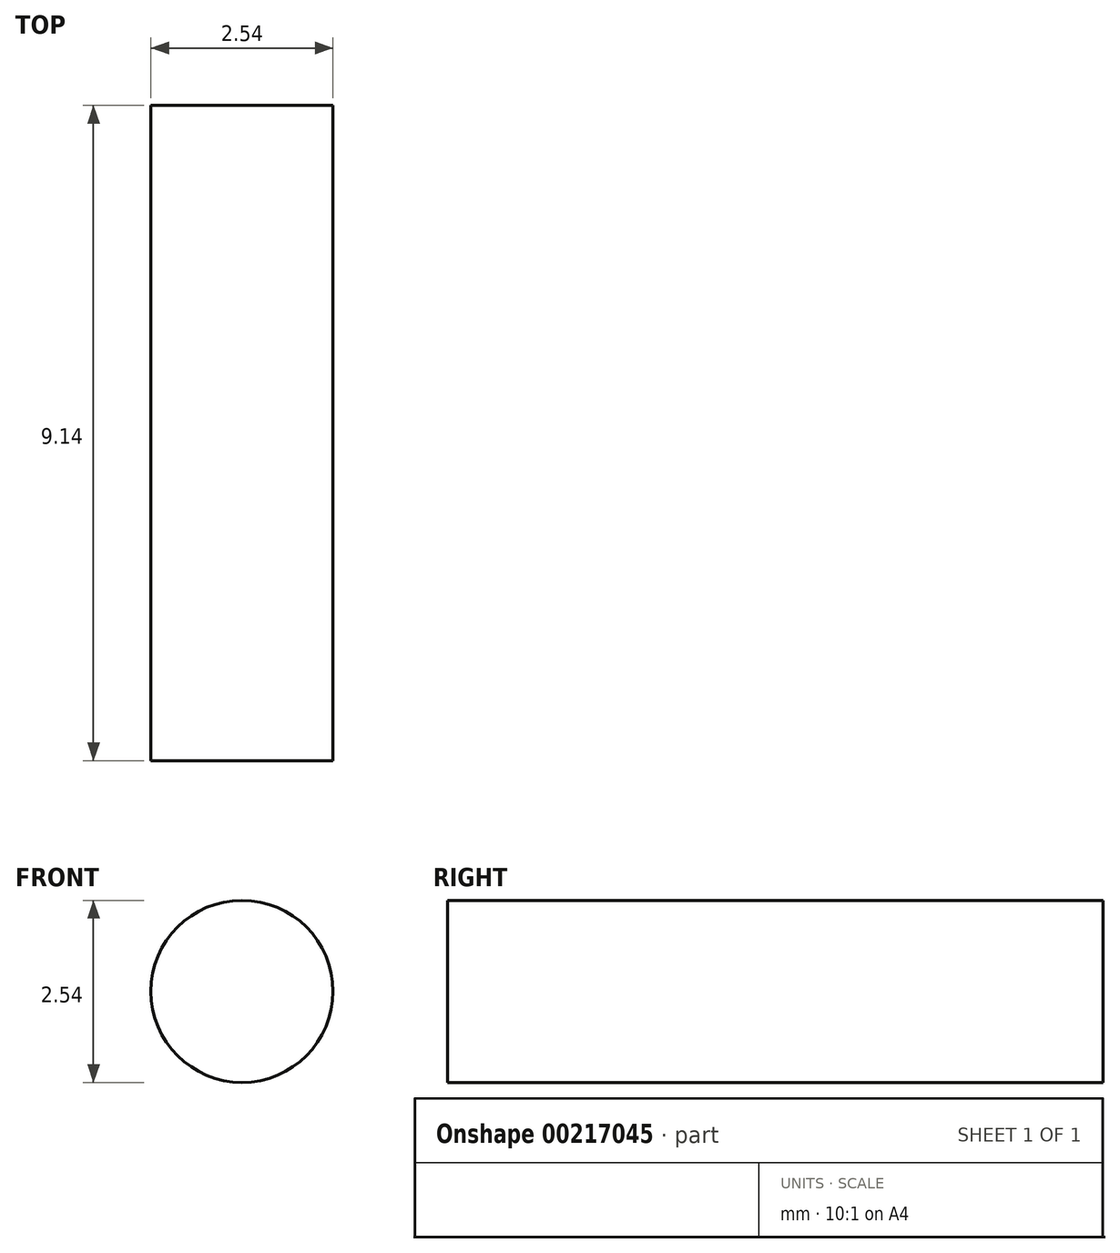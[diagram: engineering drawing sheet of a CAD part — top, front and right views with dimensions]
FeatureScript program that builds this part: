
annotation { "Feature Type Name" : "Feature", "Feature Type Description" : "" }
export const myFeature = defineFeature(function(context is Context, id is Id, definition is map)
    precondition{}
    {
        {
            var Q0;
            Q0=qCreatedBy(makeId("Front.planeOp"),FACE);
            var sketch = newSketch(context, id + "F0", { "sketchPlane" : qUnion([Q0])});
            skCircle(sketch, "E0", {"center": v(0, 0) * mm, "radius": 1.27 * mm});
            skSolve(sketch);
        }
        {
            var Q0;
            Q0 = qSketchRegion(id + "F0", true);
            extrude(context, id + "F1", {"entities" : qUnion([Q0]), "depth" : 9.14 * mm});
        }
    });
